# Revit family: FP-Revit20-en-RF178ANJX1-RF178ANX1-RefrigeratorFreezer-90004899A-US-CA
name_source: partatom
category: Specialty Equipment
units: mm (PartAtom-declared; Revit-internal decimal feet)

## family parameters
Always vertical = Yes
Cut with Voids When Loaded = Yes
Part Type = Normal
Room Calculation Point = No
Round Connector Dimension = Use Diameter
Shared = No
Work Plane-Based = No

## types (2) — shared parameters
Chassis = Fisher & Paykel - Aluminium
Clearance = Fisher & Paykel - Clearance Required (Non-Combustible)
Clearance - Vent = Fisher & Paykel - Clearance Required (Non-Combustible)
Clearance Cavity = Yes
Door Finish = Fisher & Paykel - Stainless Steel
Door swing = Yes
Electrical Specifications = Supply: 220V - 240V, 50Hz, Service: 10A circuit
Handle finish = Fisher & Paykel - Grey, Charcoal
Left side clearance = 20 mm  [stored 0.0656168 ft]
Manufacturer = Fisher & Paykel
Product depth = 707 mm
Product height = 1725 mm  [stored 5.65945 ft]
Product width = 790 mm
Rear clearance = 30 mm  [stored 0.0984252 ft]
Right side clearance = 20 mm  [stored 0.0656168 ft]
Top vent clearance = 50 mm  [stored 0.164042 ft]
URL = www.fisherpaykel.com
Vent clearance (see planning guide for options) = Yes
zero-valued in all types: Default Elevation

## per-type parameters (varying)
| type | Description | Water Pressure | Water Supply |
| RF178ANJX1 | French Door Refrigeration with Ice | Min 150 kPa (22 psi) Max 827 kPa (120 psi) @ 68°F (20°C) | 1/4" LLDPE piping |
| RF178ANUX1 | French Door Refrigeration |  |  |

note: column(s) folded — value = type name in every type: Model

note: [stored X ft] marks values corroborated as IEEE doubles in the binary element streams (Revit-internal decimal feet)

## geometry (parser evidence)
native form markers: Sweep x15
no freeform markers — native parametric forms only
